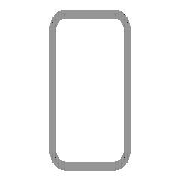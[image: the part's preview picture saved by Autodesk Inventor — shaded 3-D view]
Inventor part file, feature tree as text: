
AUTODESK INVENTOR PART (.ipt)
format: ipt  version: 2025 (Build 290162010, 162A)  size: 129,024 bytes
history: native  units: mm (DEFAULTED — no unit token found)
features: other x3, sketch x1, plane x1
ambient origin geometry x8: Origin, YZ Plane, XZ Plane, XY Plane, X Axis, Y Axis, Z Axis, Center Point
bodies: Solid1 (feature_tree), Body (feature_tree)
feature tree (5):
  other  "Driven Length"
  other  "Start plane"
  other  "End plane"
  sketch  "Sketch3"  dims[d3=1286.407mm d4=0.0mm d7=6.0mm d9=40.0mm d11=60.0mm d12=3.0mm d13=-0.0mm d14=1286.407mm d15=20.0mm d16=30.0mm d17=90.0deg d18=1286.407mm]
  plane  "Work Plane3"
